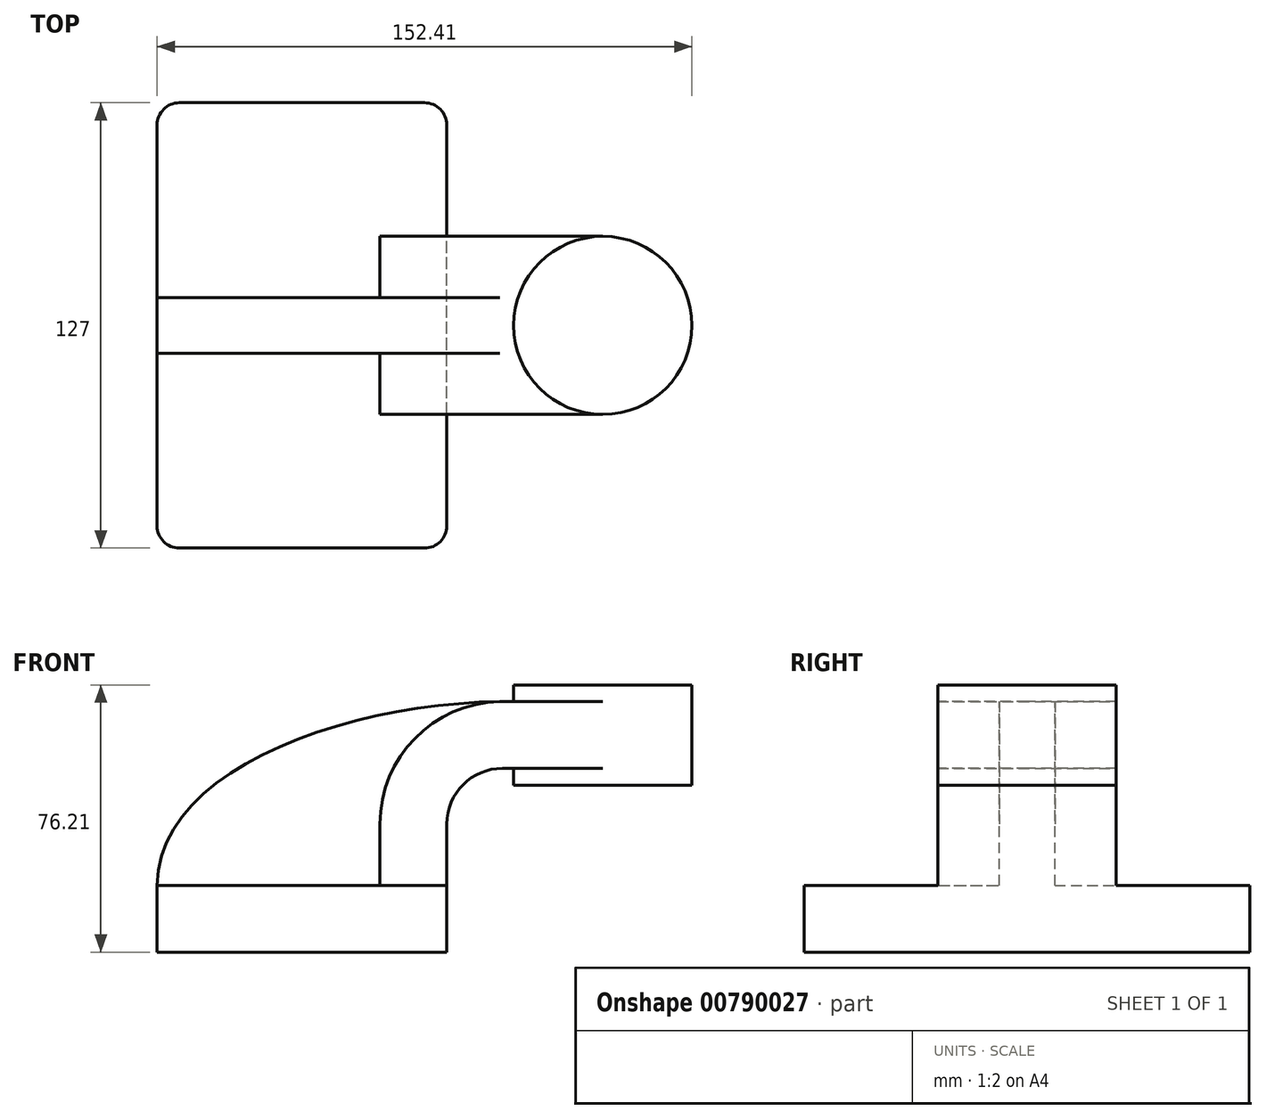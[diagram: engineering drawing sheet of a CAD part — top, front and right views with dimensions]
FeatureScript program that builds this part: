
annotation { "Feature Type Name" : "Feature", "Feature Type Description" : "" }
export const myFeature = defineFeature(function(context is Context, id is Id, definition is map)
    precondition{}
    {
        {
            var Q0;
            Q0=qCreatedBy(makeId("Front.planeOp"),FACE);
            var sketch = newSketch(context, id + "F0", { "sketchPlane" : qUnion([Q0])});
            skLineSegment(sketch, "E0.bottom", {"start": v(41.28, -9.52) * mm, "end": v(-41.28, -9.53) * mm});
            skLineSegment(sketch, "E0.top", {"start": v(41.28, 9.53) * mm, "end": v(-41.28, 9.52) * mm});
            skLineSegment(sketch, "E0.left", {"start": v(41.28, -9.53) * mm, "end": v(41.28, 9.53) * mm});
            skLineSegment(sketch, "E0.right", {"start": v(-41.28, -9.53) * mm, "end": v(-41.28, 9.52) * mm});
            skPoint(sketch, "E0.middle", {"position": v(0, 0) * mm});
            skLineSegment(sketch, "E1.bottom", {"start": v(111.12, 38.1) * mm, "end": v(60.32, 38.1) * mm});
            skLineSegment(sketch, "E1.top", {"start": v(111.12, 66.68) * mm, "end": v(60.32, 66.68) * mm});
            skLineSegment(sketch, "E1.left", {"start": v(111.12, 38.1) * mm, "end": v(111.12, 66.68) * mm});
            skLineSegment(sketch, "E1.right", {"start": v(60.32, 38.1) * mm, "end": v(60.32, 66.68) * mm});
            skPoint(sketch, "E1.middle", {"position": v(85.72, 52.39) * mm});
            skPoint(sketch, "E2.endSnap0", {"position": v(85.72, 38.1) * mm});
            skLineSegment(sketch, "E3", {"start": v(41.28, 9.53) * mm, "end": v(41.28, 27) * mm});
            skArc(sketch, "E4", {"start": v(41.28, 27) * mm, "mid": v(45.92, 38.23) * mm, "end": v(57.15, 42.88) * mm});
            skLineSegment(sketch, "E5", {"start": v(57.15, 42.88) * mm, "end": v(85.72, 42.88) * mm});
            skLineSegment(sketch, "E6.0", {"start": v(57.15, 61.93) * mm, "end": v(85.72, 61.93) * mm});
            skArc(sketch, "E6.1", {"start": v(22.23, 27) * mm, "mid": v(32.45, 51.7) * mm, "end": v(57.15, 61.93) * mm});
            skLineSegment(sketch, "E6.2", {"start": v(22.23, 9.53) * mm, "end": v(22.23, 27) * mm});
            skLineSegment(sketch, "E7", {"start": v(85.72, 38.1) * mm, "end": v(85.72, 66.68) * mm});
            skFitSpline(sketch, "E8", {"points": [v(-41.28, 9.52) * mm, v(57.15, 61.93) * mm], "startDerivative": vector(0.85, 99.59) * mm, "endDerivative": vector(132.84, 1.16) * mm});
            skSolve(sketch);
        }
        {
            var Q0;
            Q0=makeQuery(id+"F0.imprint","IMPRINT",FACE,{"disambiguationData":[TD([[makeQuery(id+"F0.imprint","IMPRINT",EDGE,{"derivedFrom":sQuery(id+"F0.wireOp",EDGE,"E0.bottom")}),-1.0]])]});
            extrude(context, id + "F1", {"entities" : qUnion([Q0]), "endBound" : BoundingType.SYMMETRIC, "depth" : 127 * mm, "offsetDistance" : 25.4 * mm});
        }
        {
            var Q0;
            {var subQ1=sQuery(id+"F0.wireOp",EDGE,"E3");Q0=makeQuery(id+"F0.imprint","IMPRINT",FACE,{"disambiguationData":[TD([[makeQuery(id+"F0.imprint","IMPRINT",EDGE,{"derivedFrom":subQ1}),1.0]])]});}
            var Q1;
            {var subQ0=sQuery(id+"F0.wireOp",EDGE,"E5");var subQ1=sQuery(id+"F0.wireOp",EDGE,"E1.right");var subQ2=makeQuery(id+"F0.imprint","INTERSECT",VERTEX,{"derivedFrom":[subQ1,subQ0]});Q1=makeQuery(id+"F0.imprint","IMPRINT",FACE,{"disambiguationData":[TD([[makeQuery(id+"F0.imprint","IMPRINT",EDGE,{"disambiguationData":[TD([[subQ2,-1.0]])],"derivedFrom":subQ1}),-1.0]])]});}
            extrude(context, id + "F2", {"entities" : qUnion([Q0, Q1]), "operationType" : NewBodyOperationType.ADD, "endBound" : BoundingType.SYMMETRIC, "depth" : 50.8 * mm, "offsetDistance" : 25.4 * mm});
        }
        {
            var Q0;
            {var subQ3=sQuery(id+"F0.wireOp",EDGE,"E6.2");Q0=makeQuery(id+"F0.imprint","IMPRINT",FACE,{"disambiguationData":[TD([[makeQuery(id+"F0.imprint","IMPRINT",EDGE,{"derivedFrom":subQ3}),1.0]])]});}
            extrude(context, id + "F3", {"entities" : qUnion([Q0]), "operationType" : NewBodyOperationType.ADD, "endBound" : BoundingType.SYMMETRIC, "depth" : 15.88 * mm, "offsetDistance" : 25.4 * mm});
        }
        {
            var Q0;
            {var subQ0=sQuery(id+"F0.wireOp",EDGE,"E1.left");Q0=makeQuery(id+"F0.imprint","IMPRINT",FACE,{"disambiguationData":[TD([[makeQuery(id+"F0.imprint","IMPRINT",EDGE,{"derivedFrom":subQ0}),1.0]])]});}
            var Q1;
            Q1=sQuery(id+"F0.wireOp",EDGE,"E7");
            revolve(context, id + "F4", {"operationType" : NewBodyOperationType.ADD, "surfaceOperationType" : NewSurfaceOperationType.NEW, "entities" : qUnion([Q0]), "axis" : qUnion([Q1]), "revolveType" : RevolveType.FULL});
        }
        {
            var Q0;
            Q0=makeQuery(id+"F1.opExtrude","CAP_EDGE",EDGE,{"disambiguationData":[OSD([sQuery(id+"F0.wireOp",EDGE,"E0.left")])],"isStart":false});
            var Q1;
            Q1=makeQuery(id+"F1.opExtrude","CAP_EDGE",EDGE,{"disambiguationData":[OSD([sQuery(id+"F0.wireOp",EDGE,"E0.left")])],"isStart":true});
            var Q2;
            Q2=makeQuery(id+"F1.opExtrude","CAP_EDGE",EDGE,{"disambiguationData":[OSD([sQuery(id+"F0.wireOp",EDGE,"E0.right")])],"isStart":true});
            var Q3;
            Q3=makeQuery(id+"F1.opExtrude","CAP_EDGE",EDGE,{"disambiguationData":[OSD([sQuery(id+"F0.wireOp",EDGE,"E0.right")])],"isStart":false});
            fillet(context, id + "F5", {"entities" : qUnion([Q0, Q1, Q2, Q3]), "radius" : 6.35 * mm, "tangentPropagation" : true, "allowEdgeOverflow" : false});
        }
    });
